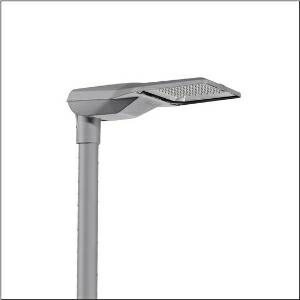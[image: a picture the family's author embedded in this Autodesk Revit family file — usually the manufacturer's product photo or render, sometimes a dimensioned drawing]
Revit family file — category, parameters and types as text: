
# Revit family: streetlight_sl_21_iq_midi___p0_8ab_5xe3r31g08mb_fd1f
name_source: partatom
category: Lighting Fixtures
units: mm (PartAtom-declared; Revit-internal decimal feet)

## family parameters
Cut with Voids When Loaded = No
Host = Face
Light Source = No
Part Type = Normal
Room Calculation Point = No
Round Connector Dimension = Use Diameter
Shared = No

## types (1)
- --- (1 x LED, 16930 lm, 146.7 W, 3000K)
    Apparent Load = 147 VA
    CIE Flux Codes = 36 71 98 100 100
    Color Rendering = 70
    Color Temperature = 3000K
    Default Elevation = 1800 mm
    Description = Streetlight SL 21 iQ midi, mast luminaire, primary light control with lens, of PMMA, primary optical cover: cover, of toughened safety glass, transparent, light distribution: P0.8aB, light emission: direct distribution, primary light characteristic: asymmetric, installation type: post-top, side-entry, LED, High Power LED, rated luminous flux: 16.930lm, luminous efficacy: 115lm/W, light colour: 730, colour temperature: 3000K, control gear: iQ Street-Remote, control: pre-setting: linear dimming characteristic, Street-Remote, Auto-Match, Temp-Guard, Lumen-Switch, Night-Set, Smart-Wire, Light-Fading, Desk-Remote (wireless, voltage-free reading and setting of iQ features in the workshop via application-optimized NFC function/RFID function), optimised constant luminous flux control (CLO 2.0), mains connection: 230..240V, AC, 50/60Hz, start of lifetime: 147W, end of service life: 161W, reduction: 62W, luminaire housing, of diecast aluminium, powder-coated, SITECO metallic grey (DB 702S), corrosivity category C5 high according to DIN EN ISO 12944, please order mast flange separately, inclination adjustable: 0°, 5°, 10°, 15°, sealing non-destructively replaceable, multi-level sealing system, length: 644mm, width: 335mm, height: 110mm, mast flange for spigot size: 42mm (side-entry): 5XC10008XM4, 60/48mm (side-entry/post-top): 5XC10108XM2, 76/60mm (side-entry/post-top): 5XC10108XM1, mounting height: 4..8m, protection rating (complete): IP66, insulation class (complete): insulation class II (safety insulation), certification: CE, ENEC, ENEC+, VDE, impact resistance: IK10, permissible operating ambient temperature for outdoor applications: -40..+50°C, standard-compliant lighting for roads and squares, packaging unit: 1 piece

Light Distribution: P0.8aB
    Height = 111 mm
    Lamp = 1 x LED
    Lamp Light Flux = 16930 lm
    Lamp Power = 146.7 W
    Lamp count = 1
    Length = 644 mm
    Luminous efficacy = 115 lm/W
    Manufacturer = Siteco
    ModVariant = No
    Model = 5XE3R31G08MB
    Number of Poles = 1
    OnlyDefault = Yes
    Power Factor = 1
    Product Name = Streetlight SL 21 iQ midi | P0.8aB
    Product group = mast luminaire | pylon top
    ProductGroupID = 6100
    Protection Class = Protection class II
    Protection Degree = IP 66
    RLX_Detail_Level = 1
    RLX_Emergency_Light_Flux = 0 lm
    RLX_Emergency_Type = 0
    RLX_Emergency_Type_DB = No
    RlxData = <blob elided: 90509 chars, md5=002aeac9>
    Socket = socket
    Standby Power = 0 W
    System Light Flux = 16931 lm
    System Power = 147 W
    Type Comments = factory setting: luminous flux: 100 % | dim-lin: 254 | 753 mA
    Type Image = l_1004298.jpg
    URL = http://relux.com
    VarID = @adj_082111
    Voltage = 0 V
    Weight = 0.00 kg
    Width = 336 mm

## geometry (parser evidence)
native form markers: Blend x4, Sweep x11
no freeform markers — native parametric forms only
